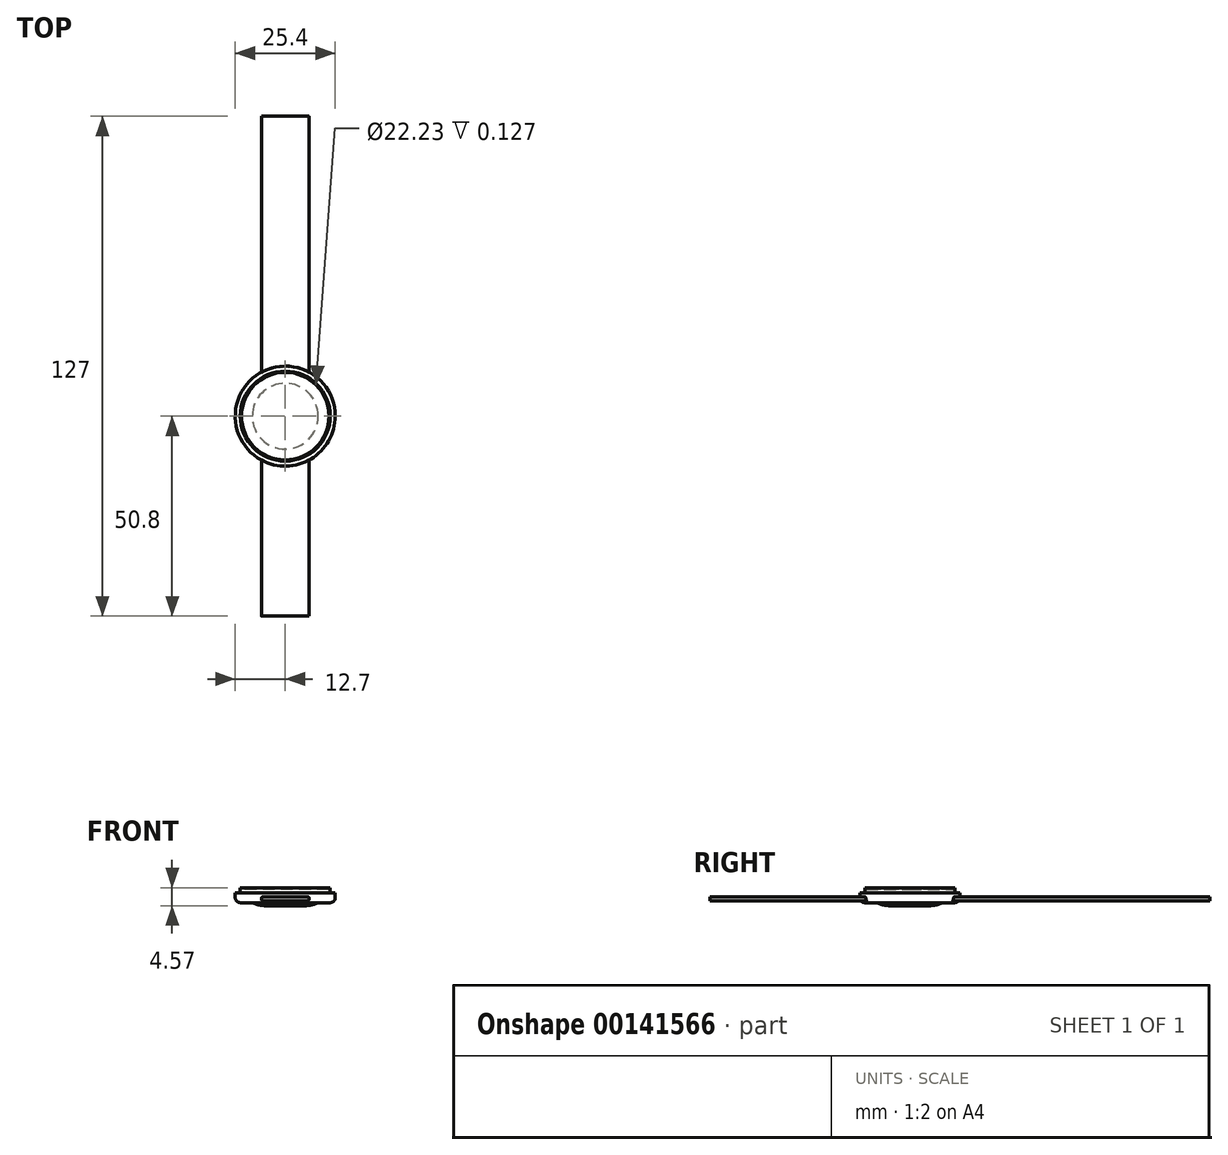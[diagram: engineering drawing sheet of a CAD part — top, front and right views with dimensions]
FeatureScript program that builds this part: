
annotation { "Feature Type Name" : "Feature", "Feature Type Description" : "" }
export const myFeature = defineFeature(function(context is Context, id is Id, definition is map)
    precondition{}
    {
        {
            var Q0;
            Q0=qCreatedBy(makeId("Top.planeOp"),FACE);
            var sketch = newSketch(context, id + "F0", { "sketchPlane" : qUnion([Q0])});
            skCircle(sketch, "E0", {"center": v(0, 0) * mm, "radius": 12.7 * mm});
            skCircle(sketch, "E1", {"center": v(0, 0) * mm, "radius": 11.43 * mm});
            skCircle(sketch, "E2", {"center": v(0, 0) * mm, "radius": 11.11 * mm});
            skSolve(sketch);
        }
        {
            var Q0;
            Q0=makeQuery(id+"F0.imprint","IMPRINT",FACE,{"disambiguationData":[TD([[makeQuery(id+"F0.imprint","IMPRINT",EDGE,{"derivedFrom":sQuery(id+"F0.wireOp",EDGE,"E1")}),1.0]])]});
            extrude(context, id + "F1", {"entities" : qUnion([Q0]), "depth" : 3.8 * mm});
        }
        {
            var Q0;
            Q0=makeQuery(id+"F0.imprint","IMPRINT",FACE,{"disambiguationData":[TD([[makeQuery(id+"F0.imprint","IMPRINT",EDGE,{"derivedFrom":sQuery(id+"F0.wireOp",EDGE,"E0")}),1.0]])]});
            extrude(context, id + "F2", {"entities" : qUnion([Q0]), "operationType" : NewBodyOperationType.ADD, "depth" : 2.54 * mm});
        }
        {
            var Q0;
            Q0=makeQuery(id+"F2.opExtrude","CAP_EDGE",EDGE,{"disambiguationData":[OSD([sQuery(id+"F0.wireOp",EDGE,"E0")])],"isStart":true});
            fillet(context, id + "F3", {"entities" : qUnion([Q0]), "radius" : 1.27 * mm, "tangentPropagation" : true, "allowEdgeOverflow" : false});
        }
        {
            var Q0;
            Q0=qCreatedBy(makeId("Front.planeOp"),FACE);
            var sketch = newSketch(context, id + "F4", { "sketchPlane" : qUnion([Q0])});
            skLineSegment(sketch, "E3.bottom", {"start": v(6.04, 1.5) * mm, "end": v(-6.04, 1.5) * mm});
            skLineSegment(sketch, "E3.top", {"start": v(6.04, 0.49) * mm, "end": v(-6.04, 0.49) * mm});
            skLineSegment(sketch, "E3.left", {"start": v(6.04, 1.5) * mm, "end": v(6.04, 0.49) * mm});
            skLineSegment(sketch, "E3.right", {"start": v(-6.04, 1.5) * mm, "end": v(-6.04, 0.49) * mm});
            skPoint(sketch, "E3.middle", {"position": v(0, 1) * mm});
            skSolve(sketch);
        }
        {
            var Q0;
            Q0=makeQuery(id+"F4.imprint","IMPRINT",FACE,{"disambiguationData":[TD([[makeQuery(id+"F4.imprint","IMPRINT",EDGE,{"derivedFrom":sQuery(id+"F4.wireOp",EDGE,"E3.bottom")}),1.0]])]});
            extrude(context, id + "F5", {"entities" : qUnion([Q0]), "depth" : 50.8 * mm});
        }
        {
            var Q0;
            Q0=makeQuery(id+"F5.opExtrude","CAP_FACE",FACE,{"disambiguationData":[OSD([sQuery(id+"F4.wireOp",EDGE,"E3.bottom"),sQuery(id+"F4.wireOp",EDGE,"E3.top"),sQuery(id+"F4.wireOp",EDGE,"E3.left"),sQuery(id+"F4.wireOp",EDGE,"E3.right")])],"isStart":true});
            extrude(context, id + "F6", {"entities" : qUnion([Q0]), "operationType" : NewBodyOperationType.ADD, "depth" : 76.2 * mm});
        }
        {
            var Q0;
            {var subQ0=sQuery(id+"F4.wireOp",EDGE,"E3.left");var subQ1=sQuery(id+"F4.wireOp",EDGE,"E3.bottom");Q0=makeQuery(id+"F6.boolean.opBoolean","MERGE",EDGE,{"derivedFrom":[makeQuery(id+"F5.opExtrude","SWEPT_EDGE",EDGE,{"disambiguationData":[OSD([subQ1,subQ0])]}),makeQuery(id+"F6.opExtrude","SWEPT_EDGE",EDGE,{"disambiguationData":[OSD([subQ1,subQ0])]})]});}
            var Q1;
            {var subQ0=sQuery(id+"F4.wireOp",EDGE,"E3.left");var subQ1=sQuery(id+"F4.wireOp",EDGE,"E3.top");Q1=makeQuery(id+"F6.boolean.opBoolean","MERGE",EDGE,{"derivedFrom":[makeQuery(id+"F5.opExtrude","SWEPT_EDGE",EDGE,{"disambiguationData":[OSD([subQ1,subQ0])]}),makeQuery(id+"F6.opExtrude","SWEPT_EDGE",EDGE,{"disambiguationData":[OSD([subQ1,subQ0])]})]});}
            var Q2;
            {var subQ0=sQuery(id+"F4.wireOp",EDGE,"E3.right");var subQ1=sQuery(id+"F4.wireOp",EDGE,"E3.bottom");Q2=makeQuery(id+"F6.boolean.opBoolean","MERGE",EDGE,{"derivedFrom":[makeQuery(id+"F5.opExtrude","SWEPT_EDGE",EDGE,{"disambiguationData":[OSD([subQ1,subQ0])]}),makeQuery(id+"F6.opExtrude","SWEPT_EDGE",EDGE,{"disambiguationData":[OSD([subQ1,subQ0])]})]});}
            var Q3;
            {var subQ0=sQuery(id+"F4.wireOp",EDGE,"E3.right");var subQ1=sQuery(id+"F4.wireOp",EDGE,"E3.top");Q3=makeQuery(id+"F6.boolean.opBoolean","MERGE",EDGE,{"derivedFrom":[makeQuery(id+"F5.opExtrude","SWEPT_EDGE",EDGE,{"disambiguationData":[OSD([subQ1,subQ0])]}),makeQuery(id+"F6.opExtrude","SWEPT_EDGE",EDGE,{"disambiguationData":[OSD([subQ1,subQ0])]})]});}
            fillet(context, id + "F7", {"entities" : qUnion([Q0, Q1, Q2, Q3]), "radius" : 0.38 * mm, "tangentPropagation" : true, "allowEdgeOverflow" : false});
        }
        {
            var Q0;
            Q0=makeQuery(id+"F0.imprint","IMPRINT",FACE,{"disambiguationData":[TD([[makeQuery(id+"F0.imprint","IMPRINT",EDGE,{"derivedFrom":sQuery(id+"F0.wireOp",EDGE,"E2")}),1.0]])]});
            extrude(context, id + "F8", {"entities" : qUnion([Q0]), "operationType" : NewBodyOperationType.ADD, "depth" : 3.43 * mm});
        }
        {
            var Q0;
            Q0=makeQuery(id+"F0.imprint","IMPRINT",FACE,{"disambiguationData":[TD([[makeQuery(id+"F0.imprint","IMPRINT",EDGE,{"derivedFrom":sQuery(id+"F0.wireOp",EDGE,"E2")}),1.0]])]});
            var sketch = newSketch(context, id + "F9", { "sketchPlane" : qUnion([Q0])});
            skCircle(sketch, "E4", {"center": v(0, 0) * mm, "radius": 8.37 * mm});
            skSolve(sketch);
        }
        {
            var Q0;
            Q0=makeQuery(id+"F9.imprint","IMPRINT",FACE,{"disambiguationData":[TD([[makeQuery(id+"F9.imprint","IMPRINT",EDGE,{"derivedFrom":sQuery(id+"F9.wireOp",EDGE,"E4")}),1.0]])]});
            extrude(context, id + "F10", {"entities" : qUnion([Q0]), "operationType" : NewBodyOperationType.ADD, "oppositeDirection" : true, "depth" : 0.76 * mm});
        }
        {
            var Q0;
            Q0=makeQuery(id+"F10.opExtrude","CAP_EDGE",EDGE,{"disambiguationData":[OSD([sQuery(id+"F9.wireOp",EDGE,"E4")])],"isStart":false});
            fillet(context, id + "F11", {"entities" : qUnion([Q0]), "radius" : 7.62 * mm, "tangentPropagation" : true, "allowEdgeOverflow" : false});
        }
        {
            var Q0;
            Q0=makeQuery(id+"F1.opExtrude","CAP_EDGE",EDGE,{"disambiguationData":[OSD([sQuery(id+"F0.wireOp",EDGE,"E2")])],"isStart":false});
            fillet(context, id + "F12", {"entities" : qUnion([Q0]), "radius" : 0.25 * mm, "tangentPropagation" : true, "allowEdgeOverflow" : false});
        }
    });
